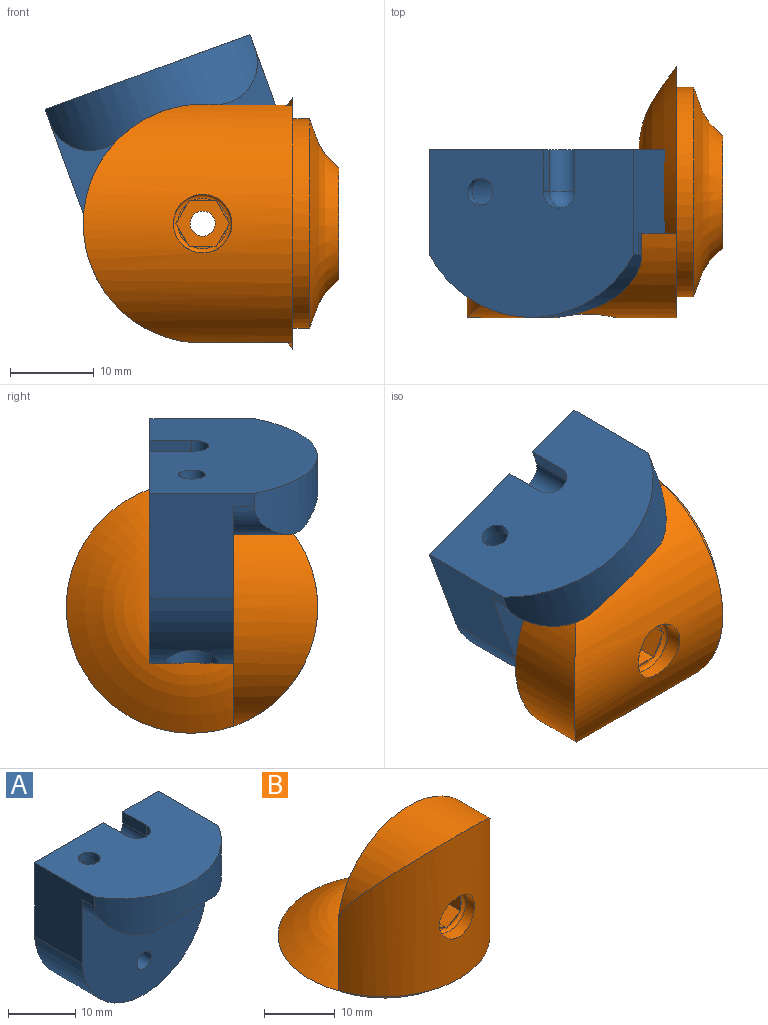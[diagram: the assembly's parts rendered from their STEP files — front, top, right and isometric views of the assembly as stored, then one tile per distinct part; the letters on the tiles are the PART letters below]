
ASSEMBLY  parts=2 mates=1
PART A: 22 faces, bbox 26x20x25.5 mm
  f0: cylinder r=1.5mm len=7.5mm, axis (0,-1,0), area 70.7mm2, adj f4,f19
  f1: cylinder r=13.03mm len=26mm, axis (0,-1,0), area 351.3mm2, adj f3,f4,f5,f6,f16
  f2: plane 26x20mm, normal (0,0,1), area 428.9mm2, adj f3,f5,f6,f7,f10,f11,f12,f13
  f3: plane 26x25.5mm, normal (0,1,0), area 543.5mm2, adj f1,f2,f5,f6,f11,f13,f14,f18
  f4: plane 26x23.76mm, normal (0,-1,0), area 434.4mm2, adj f0,f1,f5,f6,f8,f9,f20,f21
  f5: plane 13.41x12.48mm, normal (-1,0,0), area 138.5mm2, adj f1,f2,f3,f4,f7,f20
  f6: plane 13.41x12.48mm, normal (1,0,0), area 138.5mm2, adj f1,f2,f3,f4,f7,f21
  f7: cylinder r=15mm len=26mm, axis (0,0,-1), area 177.3mm2, adj f2,f5,f6,f8,f20,f21
  f8: cylinder r=14.25mm len=11.84mm, axis (0,1,0), area 117.1mm2, adj f4,f7,f20,f21
  f9: sphere r=0.6mm, area 2.3mm2, adj f4
  f10: cylinder r=1.6mm len=3.2mm, axis (0,0,1), area 15.1mm2, adj f2,f17
  f11: plane 5x2mm, normal (1,0,0), area 10mm2, adj f2,f3,f12,f14
  f12: cylinder r=2mm len=4mm, axis (0,0,1), area 12.6mm2, adj f2,f11,f13,f15
  f13: plane 5x2mm, normal (-1,0,0), area 10mm2, adj f2,f3,f12,f14
  f14: cylinder r=2mm len=5mm, axis (0,1,0), area 31.4mm2, adj f3,f11,f13,f15
  f15: sphere r=2mm, area 12.6mm2, adj f12,f14
  f16: cylinder r=3.25mm len=23.59mm, axis (0,0,-1), area 448mm2, adj f1,f17
  f17: plane 6.5x6.5mm, normal (0,0,-1), area 25.1mm2, adj f10,f16
  f18: cylinder r=3.25mm len=6.5mm, axis (0,1,0), area 51.1mm2, adj f3,f19
  f19: plane 6.5x6.5mm, normal (0,1,0), area 26.1mm2, adj f0,f18
  f20: cylinder r=5mm len=8.78mm, axis (0,1,0), area 54.9mm2, adj f4,f5,f7,f8
  f21: cylinder r=5mm len=8.78mm, axis (0,1,0), area 54.9mm2, adj f4,f6,f7,f8
PART B: 51 faces, bbox 30x30x30.5 mm
  f0: plane 1.99x1.15mm, normal (0,-1,0), area 0.4mm2, adj f45,f50
  f1: plane 1.99x1.15mm, normal (0,-1,0), area 0.4mm2, adj f44,f50
  f2: plane 2.3x0.23mm, normal (0,-1,0), area 0.4mm2, adj f43,f50
  f3: plane 1.99x1.15mm, normal (0,-1,0), area 0.4mm2, adj f42,f50
  f4: plane 1.99x1.15mm, normal (0,-1,0), area 0.4mm2, adj f41,f50
  f5: cylinder r=15mm len=28.28mm, axis (0,0,-1), area 740mm2, adj f6,f8,f15,f48
  f6: plane 28.28x25mm, normal (0,1,0), area 485.1mm2, adj f5,f7,f15,f16,f17,f19,f21,f23
  f7: revolved ~30x30mm, area 480.3mm2, adj f6,f8,f14
  f8: plane 30x30mm, normal (0,0,-1), area 216mm2, adj f5,f7,f9
  f9: cylinder r=12.5mm len=25mm, axis (0,0,1), area 157.1mm2, adj f8,f10
  f10: revolved ~25x25mm, area 407.9mm2, adj f9,f11
  f11: plane 13.4x13.4mm, normal (0,0,-1), area 108.9mm2, adj f10,f12
  f12: cylinder r=3.2mm len=6.4mm, axis (0,0,1), area 60.3mm2, adj f11,f13
  f13: plane 10x10mm, normal (0,0,1), area 46.4mm2, adj f12,f14
  f14: cylinder r=5mm len=10mm, axis (0,0,1), area 219.9mm2, adj f7,f13
  f15: cylinder r=14.25mm len=28.28mm, axis (0,1,0), area 248.3mm2, adj f5,f6
  f16: cylinder r=1.5mm len=4mm, axis (0,1,0), area 37.7mm2, adj f6,f47
  f17: cylinder r=1mm len=2mm, axis (0,1,0), area 12.6mm2, adj f6,f18
  f18: plane 2x2mm, normal (0,1,0), area 3.1mm2, adj f17
  f19: cylinder r=1mm len=2mm, axis (0,1,0), area 12.6mm2, adj f6,f20
  f20: plane 2x2mm, normal (0,1,0), area 3.1mm2, adj f19
  f21: cylinder r=1mm len=2mm, axis (0,1,0), area 12.6mm2, adj f6,f22
  f22: plane 2x2mm, normal (0,1,0), area 3.1mm2, adj f21
  f23: cylinder r=1mm len=2mm, axis (0,1,0), area 12.6mm2, adj f6,f24
  f24: plane 2x2mm, normal (0,1,0), area 3.1mm2, adj f23
  f25: cylinder r=1mm len=2mm, axis (0,1,0), area 12.6mm2, adj f6,f26
  f26: plane 2x2mm, normal (0,1,0), area 3.1mm2, adj f25
  f27: cylinder r=1mm len=2mm, axis (0,1,0), area 12.6mm2, adj f6,f28
  f28: plane 2x2mm, normal (0,1,0), area 3.1mm2, adj f27
  f29: cylinder r=1mm len=2mm, axis (0,1,0), area 12.6mm2, adj f6,f30
  f30: plane 2x2mm, normal (0,1,0), area 3.1mm2, adj f29
  f31: cylinder r=1mm len=2mm, axis (0,1,0), area 12.6mm2, adj f6,f32
  f32: plane 2x2mm, normal (0,1,0), area 3.1mm2, adj f31
  f33: cylinder r=1mm len=2mm, axis (0,1,0), area 12.6mm2, adj f6,f34
  f34: plane 2x2mm, normal (0,1,0), area 3.1mm2, adj f33
  f35: cylinder r=1mm len=2mm, axis (0,1,0), area 12.6mm2, adj f6,f36
  f36: plane 2x2mm, normal (0,1,0), area 3.1mm2, adj f35
  f37: cylinder r=1mm len=2mm, axis (0,1,0), area 12.6mm2, adj f6,f38
  f38: plane 2x2mm, normal (0,1,0), area 3.1mm2, adj f37
  f39: cylinder r=1mm len=2mm, axis (0,1,0), area 12.6mm2, adj f6,f40
  f40: plane 2x2mm, normal (0,1,0), area 3.1mm2, adj f39
  f41: plane 3.56x2.79mm, normal (-0.5,0,0.87), area 11.2mm2, adj f4,f42,f46,f47,f50
  f42: plane 3.56x2.79mm, normal (0.5,0,0.87), area 11.2mm2, adj f3,f41,f43,f47,f50
  f43: plane 3.56x3.22mm, normal (1,0,0), area 11.2mm2, adj f2,f42,f44,f47,f50
  f44: plane 3.56x2.79mm, normal (0.5,0,-0.87), area 11.2mm2, adj f1,f43,f45,f47,f50
  f45: plane 3.56x2.79mm, normal (-0.5,0,-0.87), area 11.2mm2, adj f0,f44,f46,f47,f50
  f46: plane 3.56x3.22mm, normal (-1,0,0), area 11.2mm2, adj f41,f45,f47,f49,f50
  f47: plane 6.4x5.54mm, normal (0,-1,0), area 19.5mm2, adj f16,f41,f42,f43,f44,f45,f46
  f48: cylinder r=3.5mm len=7mm, axis (0,-1,0), area 39.5mm2, adj f5,f50
  f49: plane 2.3x0.23mm, normal (0,-1,0), area 0.4mm2, adj f46,f50
  f50: torus R=3mm, axis (0,1,0), area 15.9mm2, adj f0,f1,f2,f3,f4,f41,f42,f43
PLACE A rot(axis=(0,-1,0),20deg) t=(9.81,9.48,-4.19)mm
PLACE B rot(axis=(0,-1,0),90deg) t=(13.92,9.48,1.69)mm
MATE revolute A.f0 <-> B.f48  axis (0,-1,0) through (7.67,4.48,1.69)mm
